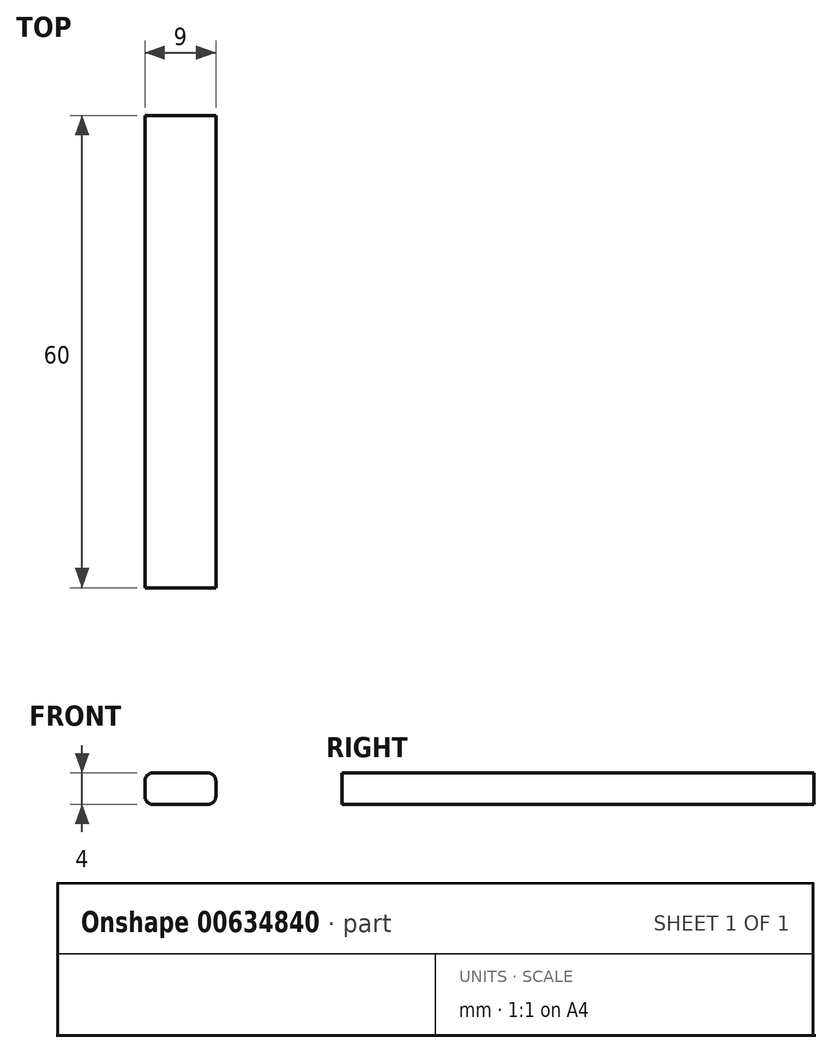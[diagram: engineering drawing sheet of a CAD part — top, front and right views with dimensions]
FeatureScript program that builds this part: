
annotation { "Feature Type Name" : "Feature", "Feature Type Description" : "" }
export const myFeature = defineFeature(function(context is Context, id is Id, definition is map)
    precondition{}
    {
        {
            var Q0;
            Q0=qCreatedBy(makeId("Front.planeOp"),FACE);
            var sketch = newSketch(context, id + "F0", { "sketchPlane" : qUnion([Q0])});
            skLineSegment(sketch, "E0.bottom", {"start": v(-23.27, -14.9) * mm, "end": v(-16.27, -14.9) * mm});
            skLineSegment(sketch, "E0.top", {"start": v(-23.27, -18.9) * mm, "end": v(-16.27, -18.9) * mm});
            skLineSegment(sketch, "E0.left", {"start": v(-24.27, -15.9) * mm, "end": v(-24.27, -17.9) * mm});
            skLineSegment(sketch, "E0.right", {"start": v(-15.27, -15.9) * mm, "end": v(-15.27, -17.9) * mm});
            skPoint(sketch, "E1.visualSharp", {"position": v(-24.27, -14.9) * mm});
            skArc(sketch, "E1.filletArc", {"start": v(-23.27, -14.9) * mm, "mid": v(-23.98, -15.2) * mm, "end": v(-24.27, -15.9) * mm});
            skPoint(sketch, "E2.visualSharp", {"position": v(-15.27, -14.9) * mm});
            skArc(sketch, "E2.filletArc", {"start": v(-15.27, -15.9) * mm, "mid": v(-15.57, -15.2) * mm, "end": v(-16.27, -14.9) * mm});
            skPoint(sketch, "E3.visualSharp", {"position": v(-15.27, -18.9) * mm});
            skArc(sketch, "E3.filletArc", {"start": v(-16.27, -18.9) * mm, "mid": v(-15.57, -18.61) * mm, "end": v(-15.27, -17.9) * mm});
            skPoint(sketch, "E4.visualSharp", {"position": v(-24.27, -18.9) * mm});
            skArc(sketch, "E4.filletArc", {"start": v(-24.27, -17.9) * mm, "mid": v(-23.98, -18.61) * mm, "end": v(-23.27, -18.9) * mm});
            skSolve(sketch);
        }
        {
            var Q0;
            Q0=makeQuery(id+"F0.imprint","IMPRINT",FACE,{"disambiguationData":[TD([[makeQuery(id+"F0.imprint","IMPRINT",EDGE,{"derivedFrom":sQuery(id+"F0.wireOp",EDGE,"E0.bottom")}),-1.0]])]});
            extrude(context, id + "F1", {"entities" : qUnion([Q0]), "depth" : 60 * mm, "offsetDistance" : 25 * mm});
        }
    });
